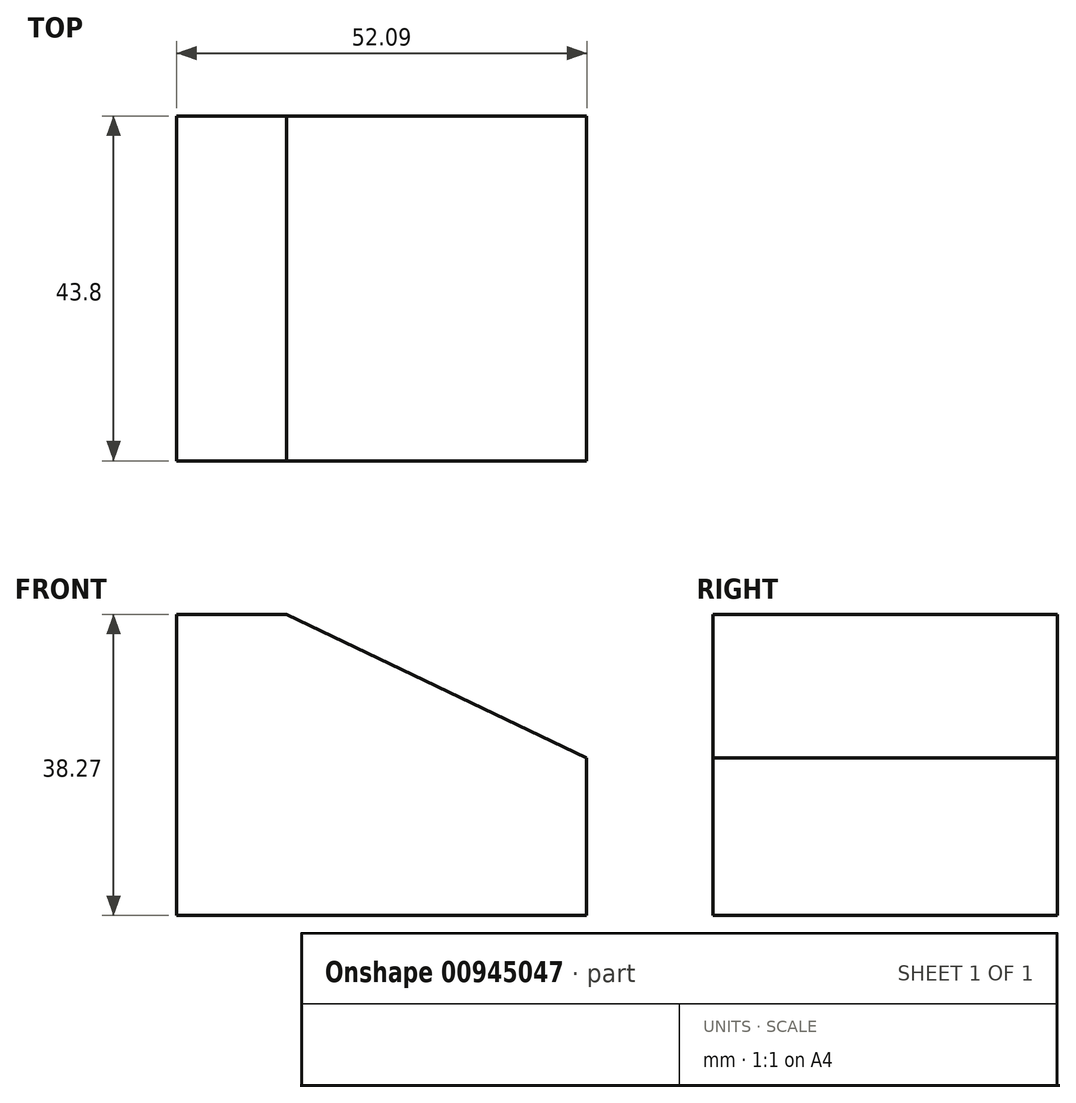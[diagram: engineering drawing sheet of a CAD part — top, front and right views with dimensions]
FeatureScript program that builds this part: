
annotation { "Feature Type Name" : "Feature", "Feature Type Description" : "" }
export const myFeature = defineFeature(function(context is Context, id is Id, definition is map)
    precondition{}
    {
        {
            var Q0;
            Q0=qCreatedBy(makeId("Front.planeOp"),FACE);
            var sketch = newSketch(context, id + "F0", { "sketchPlane" : qUnion([Q0])});
            skLineSegment(sketch, "E0", {"start": v(0, 0) * mm, "end": v(0, 38.27) * mm});
            skLineSegment(sketch, "E1", {"start": v(0, 38.27) * mm, "end": v(13.95, 38.27) * mm});
            skLineSegment(sketch, "E2", {"start": v(13.95, 38.27) * mm, "end": v(52.09, 20.03) * mm});
            skLineSegment(sketch, "E3", {"start": v(52.09, 20.03) * mm, "end": v(52.09, 0) * mm});
            skLineSegment(sketch, "E4", {"start": v(52.09, 0) * mm, "end": v(0, 0) * mm});
            skSolve(sketch);
        }
        {
            var Q0;
            Q0 = qSketchRegion(id + "F0", true);
            extrude(context, id + "F1", {"entities" : qUnion([Q0]), "depth" : 43.8 * mm, "offsetDistance" : 25 * mm});
        }
    });
